# Revit family: e4426eff-8cfc-4998-890a-6ba909027ef1
name_source: partatom
category: Specialty Equipment
revit_build: Autodesk Revit 2016 (Build: 20161004_0715(x64)
units: mm (PartAtom-declared; Revit-internal decimal feet)

## family parameters
Always vertical = Yes
Cut with Voids When Loaded = No
OmniClass Number = 23.35.70.24.11
OmniClass Title = Suspended Ceilings
Part Type = Normal
Room Calculation Point = No
Round Connector Dimension = Use Diameter
Shared = No
Work Plane-Based = Yes

## types (1)
- Parametric
    04 CSI = 09 51 00
    95 CSI = 09510
    Additional Resources Note = Product details, finishes, construction details, and more can be accessed on the Product Page URL.
    Angle = 60.00°
    Apothem = 62 91/256"
    Arc Length = 75 23/64"
    Assembly Code = C3030210
    CTRL Angle = 60.00°
    CTRL Half Angle = 30.00°
    CTRL Radius = 72"
    Chord Length = 72"
    Default Elevation = 0"
    Description = Curved High Profile Baffle
    Different Colors Available = Yes
    EPD URL = In Process
    Fire Rating = Class A
    Flame Spread Index = ≤ 25
    GREENGUARD Certified = Yes
    GREENGUARD URL = http://assets.hunterdouglascontract.com
    HPD URL = In Process
    Height = 6 3/8"
    High Durability = Yes
    Humidity and Sag Resistant = Yes
    Light Reflectance Average = 0
    Manufacturer = Hunter Douglas Luxalon Metal Ceilings
    Manufacturer Fax = 770-806-0214
    Material = Aluminum
    Minimum Radius = 48"
    Model = Aero Profile
    Mold Resistant = Yes
    Offset = 9 165/256"
    Panel = Metal - HunterDouglas - Steel Stain
    Panel Length Range = 2'-20'
    Product Line = High Profile - Curved
    Product Page URL = http://www.hunterdouglascontract.com
    Radius = 72"
    Recyclable = Yes
    Recycled Content Percentage = Min 70%
    Smoke Developed Index = ≤ 50
    Subcategory = Metal – High Profile
    Technical Information = http://assets.hunterdouglascontract.com
    URL = http://www.hunterdouglascontract.com
    VOC Data URL = http://assets.hunterdouglascontract.com
    Warranty URL = http://assets.hunterdouglascontract.com

## geometry (parser evidence)
native form markers: Blend x4, Sweep x7
no freeform markers — native parametric forms only
